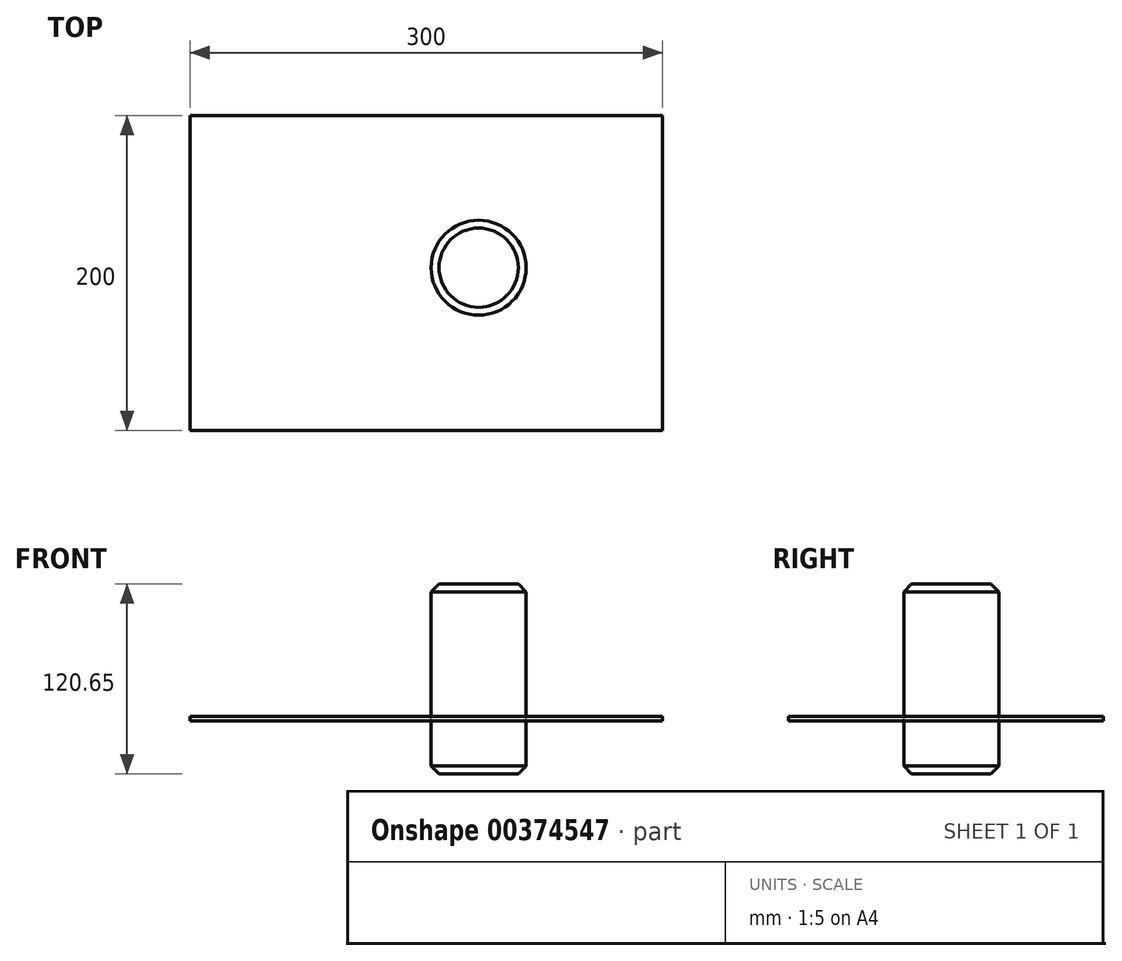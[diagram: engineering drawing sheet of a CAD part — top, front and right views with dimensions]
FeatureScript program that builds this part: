
annotation { "Feature Type Name" : "Feature", "Feature Type Description" : "" }
export const myFeature = defineFeature(function(context is Context, id is Id, definition is map)
    precondition{}
    {
        {
            var Q0;
            Q0=qCreatedBy(makeId("Front.planeOp"),FACE);
            var sketch = newSketch(context, id + "F0", { "sketchPlane" : qUnion([Q0])});
            skLineSegment(sketch, "E0", {"start": v(0, 0) * mm, "end": v(0, -33.58) * mm});
            skLineSegment(sketch, "E1", {"start": v(0, -33.58) * mm, "end": v(-30.16, -33.58) * mm});
            skLineSegment(sketch, "E2", {"start": v(-30.16, -33.58) * mm, "end": v(-30.16, 87.07) * mm});
            skLineSegment(sketch, "E3", {"start": v(-30.16, 87.07) * mm, "end": v(0, 87.07) * mm});
            skLineSegment(sketch, "E4", {"start": v(0, 87.07) * mm, "end": v(0, 0) * mm});
            skSolve(sketch);
        }
        {
            var Q0;
            Q0 = qSketchRegion(id + "F0", true);
            var Q1;
            Q1=sQuery(id+"F0.wireOp",EDGE,"E4");
            revolve(context, id + "F1", {"entities" : qUnion([Q0]), "axis" : qUnion([Q1]), "revolveType" : RevolveType.FULL});
        }
        {
            var Q0;
            Q0=makeQuery(id+"F1.opRevolve","SWEPT_EDGE",EDGE,{"disambiguationData":[OSD([sQuery(id+"F0.wireOp",EDGE,"E2"),sQuery(id+"F0.wireOp",EDGE,"E3")])]});
            var Q1;
            Q1=makeQuery(id+"F1.opRevolve","SWEPT_EDGE",EDGE,{"disambiguationData":[OSD([sQuery(id+"F0.wireOp",EDGE,"E1"),sQuery(id+"F0.wireOp",EDGE,"E2")])]});
            chamfer(context, id + "F2", {"entities" : qUnion([Q0, Q1]), "width" : 5 * mm, "tangentPropagation" : true});
        }
        {
            var Q0;
            Q0=qCreatedBy(makeId("Top.planeOp"),FACE);
            var sketch = newSketch(context, id + "F3", { "sketchPlane" : qUnion([Q0])});
            skLineSegment(sketch, "E5.bottom", {"start": v(-183.25, 96.6) * mm, "end": v(116.75, 96.6) * mm});
            skLineSegment(sketch, "E5.top", {"start": v(-183.25, -103.4) * mm, "end": v(116.75, -103.4) * mm});
            skLineSegment(sketch, "E5.left", {"start": v(-183.25, 96.6) * mm, "end": v(-183.25, -103.4) * mm});
            skLineSegment(sketch, "E5.right", {"start": v(116.75, 96.6) * mm, "end": v(116.75, -103.4) * mm});
            skSolve(sketch);
        }
        {
            var Q0;
            Q0 = qSketchRegion(id + "F3", true);
            extrude(context, id + "F4", {"entities" : qUnion([Q0]), "depth" : 3 * mm, "offsetDistance" : 25 * mm});
        }
    });
